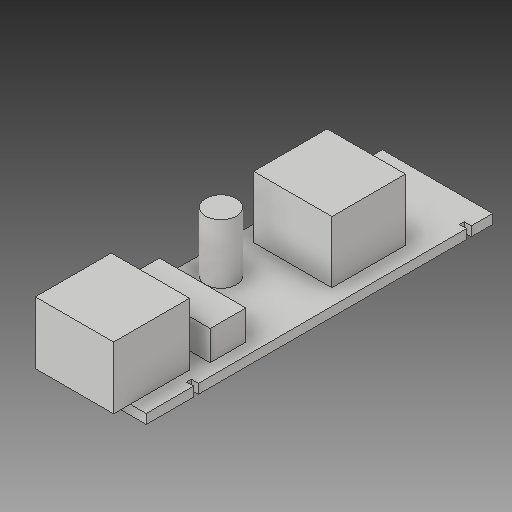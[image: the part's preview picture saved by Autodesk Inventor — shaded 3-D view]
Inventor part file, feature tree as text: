
AUTODESK INVENTOR PART (.ipt)
format: ipt  version: 2018 (Build 220112000, 112)  size: 187,904 bytes
history: native  units: in
note: dims shown in document units (in); Inventor stores cm internally (conversion verified against a paired STEP export)
features: extrude x6, sketch x6
ambient origin geometry x8: Origin, YZ Plane, XZ Plane, XY Plane, X Axis, Y Axis, Z Axis, Center Point
bodies: Solid1 (feature_tree)
feature tree (12):
  extrude  "Extrusion1"  Depth=0.9154in
  extrude  "Extrusion2"  Depth=0.1378in
  extrude  "Extrusion3"  Depth=0.6299in
  extrude  "Extrusion4"  Depth=0.6102in
  extrude  "Extrusion5"  Depth=0.5906in
  extrude  "Extrusion6"  Depth=0.374in
  sketch  "Sketch1"  dims[d0=2.874in d1=0.9154in]
  sketch  "Sketch2"  dims[d2=0.0787in d3=0.0in d4=0.1378in]
  sketch  "Sketch3"  dims[d5=0.6496in d6=0.6299in]
  sketch  "Sketch4"  dims[d7=0.5157in d8=0.0in d9=0.6102in]
  sketch  "Sketch5"  dims[d10=0.6496in d11=0.5906in]
  sketch  "Sketch6"  dims[d12=0.5118in d13=0.0in d14=0.374in d15=0.2362in d16=0.2559in d17=0.4921in d18=0.0in d19=0.2953in d20=0.7169in d21=0.1378in d22=0.2461in d23=0.0in d24=2.2638in d25=0.1969in d26=0.0394in d27=0.0591in d28=0.0in d29=0.0394in d30=0.0591in d31=0.0in d32=0.0in d33=0.0591in d34=0.0394in d35=0.0in d36=0.0591in d37=0.0394in d38=0.2461in d39=0.0in]
